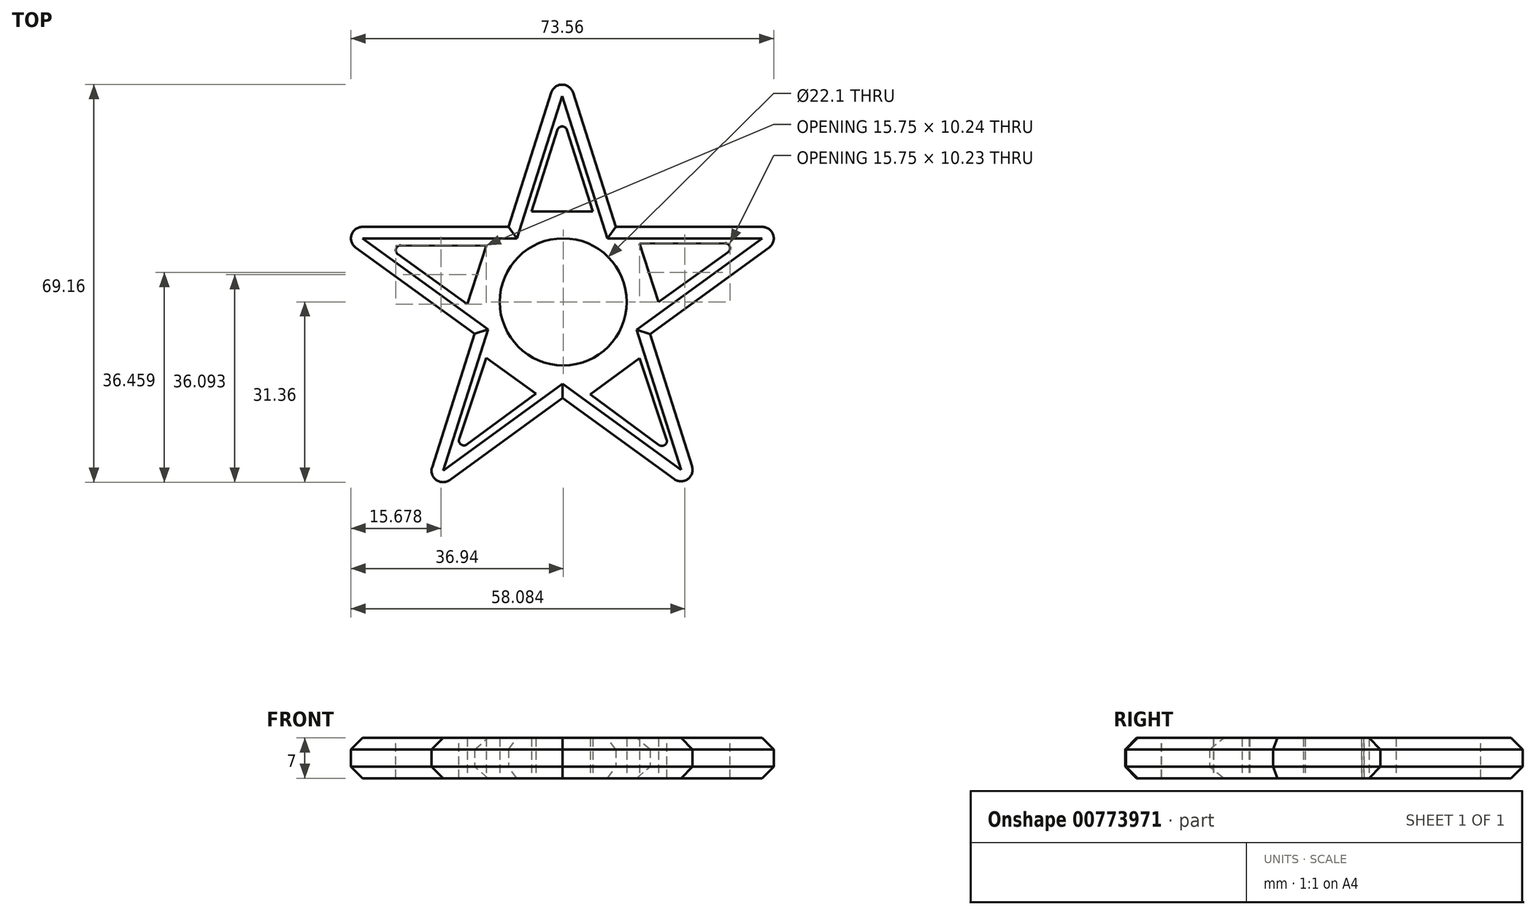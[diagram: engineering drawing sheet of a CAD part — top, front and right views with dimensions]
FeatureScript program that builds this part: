
annotation { "Feature Type Name" : "Feature", "Feature Type Description" : "" }
export const myFeature = defineFeature(function(context is Context, id is Id, definition is map)
    precondition{}
    {
        {
            var Q0;
            Q0=qCreatedBy(makeId("Top.planeOp"),FACE);
            var sketch = newSketch(context, id + "F0", { "sketchPlane" : qUnion([Q0])});
            skCircle(sketch, "E0", {"center": v(0, 0) * mm, "radius": 11.05 * mm});
            skLineSegment(sketch, "E1", {"start": v(-24.67, -34.57) * mm, "end": v(-0.2, 42.4) * mm});
            skLineSegment(sketch, "E2", {"start": v(-0.2, 42.4) * mm, "end": v(24.24, -34.41) * mm});
            skLineSegment(sketch, "E3", {"start": v(24.24, -34.41) * mm, "end": v(-41.1, 13.06) * mm});
            skLineSegment(sketch, "E4", {"start": v(-41.1, 13.06) * mm, "end": v(40.77, 13.06) * mm});
            skLineSegment(sketch, "E5", {"start": v(40.77, 13.06) * mm, "end": v(-24.67, -34.57) * mm});
            skLineSegment(sketch, "E6", {"start": v(-5.52, 15.75) * mm, "end": v(5.13, 15.75) * mm});
            skLineSegment(sketch, "E7", {"start": v(-0.2, 42.4) * mm, "end": v(-0.16, 11.05) * mm});
            skPoint(sketch, "E7.endSnap0", {"position": v(-0.16, 13.06) * mm});
            skLineSegment(sketch, "E8", {"start": v(-5.52, 15.75) * mm, "end": v(-0.19, 32.53) * mm});
            skLineSegment(sketch, "E9", {"start": v(-0.19, 32.53) * mm, "end": v(5.13, 15.75) * mm});
            skLineSegment(sketch, "E10.1.0", {"start": v(-31, 9.87) * mm, "end": v(-13.39, 9.75) * mm});
            skLineSegment(sketch, "E10.1.1", {"start": v(-16.68, -0.39) * mm, "end": v(-31, 9.87) * mm});
            skLineSegment(sketch, "E10.1.2", {"start": v(-16.68, -0.39) * mm, "end": v(-13.39, 9.75) * mm});
            skLineSegment(sketch, "E10.2.0", {"start": v(-18.97, -26.43) * mm, "end": v(-13.4, -9.72) * mm});
            skLineSegment(sketch, "E10.2.1", {"start": v(-4.79, -15.99) * mm, "end": v(-18.97, -26.43) * mm});
            skLineSegment(sketch, "E10.2.2", {"start": v(-4.79, -15.99) * mm, "end": v(-13.4, -9.72) * mm});
            skLineSegment(sketch, "E10.3.0", {"start": v(18.85, -26.52) * mm, "end": v(4.68, -16.07) * mm});
            skLineSegment(sketch, "E10.3.1", {"start": v(13.3, -9.8) * mm, "end": v(18.85, -26.52) * mm});
            skLineSegment(sketch, "E10.3.2", {"start": v(13.3, -9.8) * mm, "end": v(4.68, -16.07) * mm});
            skLineSegment(sketch, "E10.4.0", {"start": v(30.88, 10.23) * mm, "end": v(16.56, -0.02) * mm});
            skLineSegment(sketch, "E10.4.1", {"start": v(13.27, 10.12) * mm, "end": v(30.88, 10.23) * mm});
            skLineSegment(sketch, "E10.4.2", {"start": v(13.27, 10.12) * mm, "end": v(16.56, -0.02) * mm});
            skSolve(sketch);
        }
        {
            var Q0;
            Q0=qSketchRegion(id+"F0",true);
            extrude(context, id + "F1", {"entities" : qUnion([Q0]), "depth" : 7 * mm, "offsetDistance" : 25 * mm});
        }
        {
            var Q0;
            Q0=makeQuery(id+"F1.opExtrude","SWEPT_EDGE",EDGE,{"disambiguationData":[OSD([sQuery(id+"F0.wireOp",EDGE,"E1"),sQuery(id+"F0.wireOp",EDGE,"E2"),sQuery(id+"F0.wireOp",EDGE,"E7")])]});
            var Q1;
            Q1=makeQuery(id+"F1.opExtrude","SWEPT_EDGE",EDGE,{"disambiguationData":[OSD([sQuery(id+"F0.wireOp",EDGE,"E4"),sQuery(id+"F0.wireOp",EDGE,"E5")])]});
            var Q2;
            Q2=makeQuery(id+"F1.opExtrude","SWEPT_EDGE",EDGE,{"disambiguationData":[OSD([sQuery(id+"F0.wireOp",EDGE,"E2"),sQuery(id+"F0.wireOp",EDGE,"E3")])]});
            var Q3;
            Q3=makeQuery(id+"F1.opExtrude","SWEPT_EDGE",EDGE,{"disambiguationData":[OSD([sQuery(id+"F0.wireOp",EDGE,"E1"),sQuery(id+"F0.wireOp",EDGE,"E5")])]});
            var Q4;
            Q4=makeQuery(id+"F1.opExtrude","SWEPT_EDGE",EDGE,{"disambiguationData":[OSD([sQuery(id+"F0.wireOp",EDGE,"E3"),sQuery(id+"F0.wireOp",EDGE,"E4")])]});
            fillet(context, id + "F2", {"entities" : qUnion([Q0, Q1, Q2, Q3, Q4]), "radius" : 2 * mm, "tangentPropagation" : true, "allowEdgeOverflow" : false});
        }
        {
            var Q0;
            Q0=makeQuery(id+"F1.opExtrude","SWEPT_EDGE",EDGE,{"disambiguationData":[OSD([sQuery(id+"F0.wireOp",EDGE,"E10.2.0"),sQuery(id+"F0.wireOp",EDGE,"E10.2.1")])]});
            var Q1;
            Q1=makeQuery(id+"F1.opExtrude","SWEPT_EDGE",EDGE,{"disambiguationData":[OSD([sQuery(id+"F0.wireOp",EDGE,"E10.1.0"),sQuery(id+"F0.wireOp",EDGE,"E10.1.1")])]});
            var Q2;
            Q2=makeQuery(id+"F1.opExtrude","SWEPT_EDGE",EDGE,{"disambiguationData":[OSD([sQuery(id+"F0.wireOp",EDGE,"E10.3.0"),sQuery(id+"F0.wireOp",EDGE,"E10.3.1")])]});
            var Q3;
            Q3=makeQuery(id+"F1.opExtrude","SWEPT_EDGE",EDGE,{"disambiguationData":[OSD([sQuery(id+"F0.wireOp",EDGE,"E10.4.0"),sQuery(id+"F0.wireOp",EDGE,"E10.4.1")])]});
            var Q4;
            Q4=makeQuery(id+"F1.opExtrude","SWEPT_EDGE",EDGE,{"disambiguationData":[OSD([sQuery(id+"F0.wireOp",EDGE,"E7"),sQuery(id+"F0.wireOp",EDGE,"E8"),sQuery(id+"F0.wireOp",EDGE,"E9")])]});
            fillet(context, id + "F3", {"entities" : qUnion([Q0, Q1, Q2, Q3, Q4]), "radius" : 0.87 * mm, "tangentPropagation" : true, "allowEdgeOverflow" : false});
        }
        {
            var Q0;
            {var subQ0=sQuery(id+"F0.wireOp",EDGE,"E4");Q0=makeQuery(id+"F1.opExtrude","CAP_EDGE",EDGE,{"disambiguationData":[OSD([subQ0]),TDD([makeQuery(id+"F0.imprint","IMPRINT",EDGE,{"disambiguationData":[TD([[makeQuery(id+"F0.imprint","INTERSECT",VERTEX,{"derivedFrom":[sQuery(id+"F0.wireOp",EDGE,"E3"),subQ0]}),-1.0]])],"derivedFrom":subQ0})])],"isStart":false});}
            var Q1;
            {var subQ0=sQuery(id+"F0.wireOp",EDGE,"E1");Q1=makeQuery(id+"F1.opExtrude","CAP_EDGE",EDGE,{"disambiguationData":[OSD([subQ0]),TDD([makeQuery(id+"F0.imprint","IMPRINT",EDGE,{"disambiguationData":[TD([[makeQuery(id+"F0.imprint","INTERSECT",VERTEX,{"derivedFrom":[subQ0,sQuery(id+"F0.wireOp",EDGE,"E4")]}),-1.0]])],"derivedFrom":subQ0})])],"isStart":false});}
            var Q2;
            {var subQ0=sQuery(id+"F0.wireOp",EDGE,"E2");var subQ1=sQuery(id+"F0.wireOp",EDGE,"E1");Q2=makeQuery(id+"F2.opFillet","BLEND_EDGE",EDGE,{"blendedFrom":[makeQuery(id+"F1.opExtrude","SWEPT_EDGE",EDGE,{"disambiguationData":[OSD([subQ1,subQ0,sQuery(id+"F0.wireOp",EDGE,"E7")])]}),makeQuery(id+"F1.opExtrude","CAP_FACE",FACE,{"disambiguationData":[OSD([sQuery(id+"F0.wireOp",EDGE,"E0"),subQ1,subQ0,sQuery(id+"F0.wireOp",EDGE,"E3"),sQuery(id+"F0.wireOp",EDGE,"E4"),sQuery(id+"F0.wireOp",EDGE,"E5"),sQuery(id+"F0.wireOp",EDGE,"E6"),sQuery(id+"F0.wireOp",EDGE,"E8"),sQuery(id+"F0.wireOp",EDGE,"E9"),sQuery(id+"F0.wireOp",EDGE,"E10.1.0"),sQuery(id+"F0.wireOp",EDGE,"E10.1.1"),sQuery(id+"F0.wireOp",EDGE,"E10.1.2"),sQuery(id+"F0.wireOp",EDGE,"E10.2.0"),sQuery(id+"F0.wireOp",EDGE,"E10.2.1"),sQuery(id+"F0.wireOp",EDGE,"E10.2.2"),sQuery(id+"F0.wireOp",EDGE,"E10.3.0"),sQuery(id+"F0.wireOp",EDGE,"E10.3.1"),sQuery(id+"F0.wireOp",EDGE,"E10.3.2"),sQuery(id+"F0.wireOp",EDGE,"E10.4.0"),sQuery(id+"F0.wireOp",EDGE,"E10.4.1"),sQuery(id+"F0.wireOp",EDGE,"E10.4.2")])],"isStart":false})],"blendedInto":[makeQuery(id+"F1.opExtrude","CAP_FACE",FACE,{"disambiguationData":[OSD([sQuery(id+"F0.wireOp",EDGE,"E0"),subQ1,subQ0,sQuery(id+"F0.wireOp",EDGE,"E3"),sQuery(id+"F0.wireOp",EDGE,"E4"),sQuery(id+"F0.wireOp",EDGE,"E5"),sQuery(id+"F0.wireOp",EDGE,"E6"),sQuery(id+"F0.wireOp",EDGE,"E8"),sQuery(id+"F0.wireOp",EDGE,"E9"),sQuery(id+"F0.wireOp",EDGE,"E10.1.0"),sQuery(id+"F0.wireOp",EDGE,"E10.1.1"),sQuery(id+"F0.wireOp",EDGE,"E10.1.2"),sQuery(id+"F0.wireOp",EDGE,"E10.2.0"),sQuery(id+"F0.wireOp",EDGE,"E10.2.1"),sQuery(id+"F0.wireOp",EDGE,"E10.2.2"),sQuery(id+"F0.wireOp",EDGE,"E10.3.0"),sQuery(id+"F0.wireOp",EDGE,"E10.3.1"),sQuery(id+"F0.wireOp",EDGE,"E10.3.2"),sQuery(id+"F0.wireOp",EDGE,"E10.4.0"),sQuery(id+"F0.wireOp",EDGE,"E10.4.1"),sQuery(id+"F0.wireOp",EDGE,"E10.4.2")])],"isStart":false})]});}
            var Q3;
            {var subQ0=sQuery(id+"F0.wireOp",EDGE,"E2");Q3=makeQuery(id+"F1.opExtrude","CAP_EDGE",EDGE,{"disambiguationData":[OSD([subQ0]),TDD([makeQuery(id+"F0.imprint","IMPRINT",EDGE,{"disambiguationData":[TD([[makeQuery(id+"F0.imprint","INTERSECT",VERTEX,{"derivedFrom":[subQ0,sQuery(id+"F0.wireOp",EDGE,"E4")]}),1.0]])],"derivedFrom":subQ0})])],"isStart":false});}
            var Q4;
            {var subQ0=sQuery(id+"F0.wireOp",EDGE,"E4");Q4=makeQuery(id+"F1.opExtrude","CAP_EDGE",EDGE,{"disambiguationData":[OSD([subQ0]),TDD([makeQuery(id+"F0.imprint","IMPRINT",EDGE,{"disambiguationData":[TD([[makeQuery(id+"F0.imprint","INTERSECT",VERTEX,{"derivedFrom":[subQ0,sQuery(id+"F0.wireOp",EDGE,"E5")]}),1.0]])],"derivedFrom":subQ0})])],"isStart":false});}
            var Q5;
            {var subQ0=sQuery(id+"F0.wireOp",EDGE,"E5");var subQ1=sQuery(id+"F0.wireOp",EDGE,"E4");Q5=makeQuery(id+"F2.opFillet","BLEND_EDGE",EDGE,{"blendedFrom":[makeQuery(id+"F1.opExtrude","SWEPT_EDGE",EDGE,{"disambiguationData":[OSD([subQ1,subQ0])]}),makeQuery(id+"F1.opExtrude","CAP_FACE",FACE,{"disambiguationData":[OSD([sQuery(id+"F0.wireOp",EDGE,"E0"),sQuery(id+"F0.wireOp",EDGE,"E1"),sQuery(id+"F0.wireOp",EDGE,"E2"),sQuery(id+"F0.wireOp",EDGE,"E3"),subQ1,subQ0,sQuery(id+"F0.wireOp",EDGE,"E6"),sQuery(id+"F0.wireOp",EDGE,"E8"),sQuery(id+"F0.wireOp",EDGE,"E9"),sQuery(id+"F0.wireOp",EDGE,"E10.1.0"),sQuery(id+"F0.wireOp",EDGE,"E10.1.1"),sQuery(id+"F0.wireOp",EDGE,"E10.1.2"),sQuery(id+"F0.wireOp",EDGE,"E10.2.0"),sQuery(id+"F0.wireOp",EDGE,"E10.2.1"),sQuery(id+"F0.wireOp",EDGE,"E10.2.2"),sQuery(id+"F0.wireOp",EDGE,"E10.3.0"),sQuery(id+"F0.wireOp",EDGE,"E10.3.1"),sQuery(id+"F0.wireOp",EDGE,"E10.3.2"),sQuery(id+"F0.wireOp",EDGE,"E10.4.0"),sQuery(id+"F0.wireOp",EDGE,"E10.4.1"),sQuery(id+"F0.wireOp",EDGE,"E10.4.2")])],"isStart":false})],"blendedInto":[makeQuery(id+"F1.opExtrude","CAP_FACE",FACE,{"disambiguationData":[OSD([sQuery(id+"F0.wireOp",EDGE,"E0"),sQuery(id+"F0.wireOp",EDGE,"E1"),sQuery(id+"F0.wireOp",EDGE,"E2"),sQuery(id+"F0.wireOp",EDGE,"E3"),subQ1,subQ0,sQuery(id+"F0.wireOp",EDGE,"E6"),sQuery(id+"F0.wireOp",EDGE,"E8"),sQuery(id+"F0.wireOp",EDGE,"E9"),sQuery(id+"F0.wireOp",EDGE,"E10.1.0"),sQuery(id+"F0.wireOp",EDGE,"E10.1.1"),sQuery(id+"F0.wireOp",EDGE,"E10.1.2"),sQuery(id+"F0.wireOp",EDGE,"E10.2.0"),sQuery(id+"F0.wireOp",EDGE,"E10.2.1"),sQuery(id+"F0.wireOp",EDGE,"E10.2.2"),sQuery(id+"F0.wireOp",EDGE,"E10.3.0"),sQuery(id+"F0.wireOp",EDGE,"E10.3.1"),sQuery(id+"F0.wireOp",EDGE,"E10.3.2"),sQuery(id+"F0.wireOp",EDGE,"E10.4.0"),sQuery(id+"F0.wireOp",EDGE,"E10.4.1"),sQuery(id+"F0.wireOp",EDGE,"E10.4.2")])],"isStart":false})]});}
            var Q6;
            {var subQ0=sQuery(id+"F0.wireOp",EDGE,"E5");Q6=makeQuery(id+"F1.opExtrude","CAP_EDGE",EDGE,{"disambiguationData":[OSD([subQ0]),TDD([makeQuery(id+"F0.imprint","IMPRINT",EDGE,{"disambiguationData":[TD([[makeQuery(id+"F0.imprint","INTERSECT",VERTEX,{"derivedFrom":[sQuery(id+"F0.wireOp",EDGE,"E4"),subQ0]}),-1.0]])],"derivedFrom":subQ0})])],"isStart":false});}
            var Q7;
            {var subQ0=sQuery(id+"F0.wireOp",EDGE,"E2");Q7=makeQuery(id+"F1.opExtrude","CAP_EDGE",EDGE,{"disambiguationData":[OSD([subQ0]),TDD([makeQuery(id+"F0.imprint","IMPRINT",EDGE,{"disambiguationData":[TD([[makeQuery(id+"F0.imprint","INTERSECT",VERTEX,{"derivedFrom":[subQ0,sQuery(id+"F0.wireOp",EDGE,"E3")]}),1.0]])],"derivedFrom":subQ0})])],"isStart":false});}
            var Q8;
            {var subQ0=sQuery(id+"F0.wireOp",EDGE,"E3");var subQ1=sQuery(id+"F0.wireOp",EDGE,"E2");Q8=makeQuery(id+"F2.opFillet","BLEND_EDGE",EDGE,{"blendedFrom":[makeQuery(id+"F1.opExtrude","SWEPT_EDGE",EDGE,{"disambiguationData":[OSD([subQ1,subQ0])]}),makeQuery(id+"F1.opExtrude","CAP_FACE",FACE,{"disambiguationData":[OSD([sQuery(id+"F0.wireOp",EDGE,"E0"),sQuery(id+"F0.wireOp",EDGE,"E1"),subQ1,subQ0,sQuery(id+"F0.wireOp",EDGE,"E4"),sQuery(id+"F0.wireOp",EDGE,"E5"),sQuery(id+"F0.wireOp",EDGE,"E6"),sQuery(id+"F0.wireOp",EDGE,"E8"),sQuery(id+"F0.wireOp",EDGE,"E9"),sQuery(id+"F0.wireOp",EDGE,"E10.1.0"),sQuery(id+"F0.wireOp",EDGE,"E10.1.1"),sQuery(id+"F0.wireOp",EDGE,"E10.1.2"),sQuery(id+"F0.wireOp",EDGE,"E10.2.0"),sQuery(id+"F0.wireOp",EDGE,"E10.2.1"),sQuery(id+"F0.wireOp",EDGE,"E10.2.2"),sQuery(id+"F0.wireOp",EDGE,"E10.3.0"),sQuery(id+"F0.wireOp",EDGE,"E10.3.1"),sQuery(id+"F0.wireOp",EDGE,"E10.3.2"),sQuery(id+"F0.wireOp",EDGE,"E10.4.0"),sQuery(id+"F0.wireOp",EDGE,"E10.4.1"),sQuery(id+"F0.wireOp",EDGE,"E10.4.2")])],"isStart":false})],"blendedInto":[makeQuery(id+"F1.opExtrude","CAP_FACE",FACE,{"disambiguationData":[OSD([sQuery(id+"F0.wireOp",EDGE,"E0"),sQuery(id+"F0.wireOp",EDGE,"E1"),subQ1,subQ0,sQuery(id+"F0.wireOp",EDGE,"E4"),sQuery(id+"F0.wireOp",EDGE,"E5"),sQuery(id+"F0.wireOp",EDGE,"E6"),sQuery(id+"F0.wireOp",EDGE,"E8"),sQuery(id+"F0.wireOp",EDGE,"E9"),sQuery(id+"F0.wireOp",EDGE,"E10.1.0"),sQuery(id+"F0.wireOp",EDGE,"E10.1.1"),sQuery(id+"F0.wireOp",EDGE,"E10.1.2"),sQuery(id+"F0.wireOp",EDGE,"E10.2.0"),sQuery(id+"F0.wireOp",EDGE,"E10.2.1"),sQuery(id+"F0.wireOp",EDGE,"E10.2.2"),sQuery(id+"F0.wireOp",EDGE,"E10.3.0"),sQuery(id+"F0.wireOp",EDGE,"E10.3.1"),sQuery(id+"F0.wireOp",EDGE,"E10.3.2"),sQuery(id+"F0.wireOp",EDGE,"E10.4.0"),sQuery(id+"F0.wireOp",EDGE,"E10.4.1"),sQuery(id+"F0.wireOp",EDGE,"E10.4.2")])],"isStart":false})]});}
            var Q9;
            {var subQ0=sQuery(id+"F0.wireOp",EDGE,"E3");Q9=makeQuery(id+"F1.opExtrude","CAP_EDGE",EDGE,{"disambiguationData":[OSD([subQ0]),TDD([makeQuery(id+"F0.imprint","IMPRINT",EDGE,{"disambiguationData":[TD([[makeQuery(id+"F0.imprint","INTERSECT",VERTEX,{"derivedFrom":[sQuery(id+"F0.wireOp",EDGE,"E2"),subQ0]}),-1.0]])],"derivedFrom":subQ0})])],"isStart":false});}
            var Q10;
            {var subQ0=sQuery(id+"F0.wireOp",EDGE,"E5");Q10=makeQuery(id+"F1.opExtrude","CAP_EDGE",EDGE,{"disambiguationData":[OSD([subQ0]),TDD([makeQuery(id+"F0.imprint","IMPRINT",EDGE,{"disambiguationData":[TD([[makeQuery(id+"F0.imprint","INTERSECT",VERTEX,{"derivedFrom":[sQuery(id+"F0.wireOp",EDGE,"E1"),subQ0]}),1.0]])],"derivedFrom":subQ0})])],"isStart":false});}
            var Q11;
            {var subQ0=sQuery(id+"F0.wireOp",EDGE,"E1");Q11=makeQuery(id+"F1.opExtrude","CAP_EDGE",EDGE,{"disambiguationData":[OSD([subQ0]),TDD([makeQuery(id+"F0.imprint","IMPRINT",EDGE,{"disambiguationData":[TD([[makeQuery(id+"F0.imprint","INTERSECT",VERTEX,{"derivedFrom":[subQ0,sQuery(id+"F0.wireOp",EDGE,"E5")]}),-1.0]])],"derivedFrom":subQ0})])],"isStart":false});}
            var Q12;
            {var subQ0=sQuery(id+"F0.wireOp",EDGE,"E3");Q12=makeQuery(id+"F1.opExtrude","CAP_EDGE",EDGE,{"disambiguationData":[OSD([subQ0]),TDD([makeQuery(id+"F0.imprint","IMPRINT",EDGE,{"disambiguationData":[TD([[makeQuery(id+"F0.imprint","INTERSECT",VERTEX,{"derivedFrom":[subQ0,sQuery(id+"F0.wireOp",EDGE,"E4")]}),1.0]])],"derivedFrom":subQ0})])],"isStart":false});}
            var Q13;
            {var subQ0=sQuery(id+"F0.wireOp",EDGE,"E4");var subQ1=sQuery(id+"F0.wireOp",EDGE,"E3");Q13=makeQuery(id+"F2.opFillet","BLEND_EDGE",EDGE,{"blendedFrom":[makeQuery(id+"F1.opExtrude","SWEPT_EDGE",EDGE,{"disambiguationData":[OSD([subQ1,subQ0])]}),makeQuery(id+"F1.opExtrude","CAP_FACE",FACE,{"disambiguationData":[OSD([sQuery(id+"F0.wireOp",EDGE,"E0"),sQuery(id+"F0.wireOp",EDGE,"E1"),sQuery(id+"F0.wireOp",EDGE,"E2"),subQ1,subQ0,sQuery(id+"F0.wireOp",EDGE,"E5"),sQuery(id+"F0.wireOp",EDGE,"E6"),sQuery(id+"F0.wireOp",EDGE,"E8"),sQuery(id+"F0.wireOp",EDGE,"E9"),sQuery(id+"F0.wireOp",EDGE,"E10.1.0"),sQuery(id+"F0.wireOp",EDGE,"E10.1.1"),sQuery(id+"F0.wireOp",EDGE,"E10.1.2"),sQuery(id+"F0.wireOp",EDGE,"E10.2.0"),sQuery(id+"F0.wireOp",EDGE,"E10.2.1"),sQuery(id+"F0.wireOp",EDGE,"E10.2.2"),sQuery(id+"F0.wireOp",EDGE,"E10.3.0"),sQuery(id+"F0.wireOp",EDGE,"E10.3.1"),sQuery(id+"F0.wireOp",EDGE,"E10.3.2"),sQuery(id+"F0.wireOp",EDGE,"E10.4.0"),sQuery(id+"F0.wireOp",EDGE,"E10.4.1"),sQuery(id+"F0.wireOp",EDGE,"E10.4.2")])],"isStart":false})],"blendedInto":[makeQuery(id+"F1.opExtrude","CAP_FACE",FACE,{"disambiguationData":[OSD([sQuery(id+"F0.wireOp",EDGE,"E0"),sQuery(id+"F0.wireOp",EDGE,"E1"),sQuery(id+"F0.wireOp",EDGE,"E2"),subQ1,subQ0,sQuery(id+"F0.wireOp",EDGE,"E5"),sQuery(id+"F0.wireOp",EDGE,"E6"),sQuery(id+"F0.wireOp",EDGE,"E8"),sQuery(id+"F0.wireOp",EDGE,"E9"),sQuery(id+"F0.wireOp",EDGE,"E10.1.0"),sQuery(id+"F0.wireOp",EDGE,"E10.1.1"),sQuery(id+"F0.wireOp",EDGE,"E10.1.2"),sQuery(id+"F0.wireOp",EDGE,"E10.2.0"),sQuery(id+"F0.wireOp",EDGE,"E10.2.1"),sQuery(id+"F0.wireOp",EDGE,"E10.2.2"),sQuery(id+"F0.wireOp",EDGE,"E10.3.0"),sQuery(id+"F0.wireOp",EDGE,"E10.3.1"),sQuery(id+"F0.wireOp",EDGE,"E10.3.2"),sQuery(id+"F0.wireOp",EDGE,"E10.4.0"),sQuery(id+"F0.wireOp",EDGE,"E10.4.1"),sQuery(id+"F0.wireOp",EDGE,"E10.4.2")])],"isStart":false})]});}
            chamfer(context, id + "F4", {"entities" : qUnion([Q0, Q1, Q2, Q3, Q4, Q5, Q6, Q7, Q8, Q9, Q10, Q11, Q12, Q13]), "width" : 2 * mm, "tangentPropagation" : true});
        }
        {
            var Q0;
            {var subQ0=sQuery(id+"F0.wireOp",EDGE,"E4");Q0=makeQuery(id+"F1.opExtrude","CAP_EDGE",EDGE,{"disambiguationData":[OSD([subQ0]),TDD([makeQuery(id+"F0.imprint","IMPRINT",EDGE,{"disambiguationData":[TD([[makeQuery(id+"F0.imprint","INTERSECT",VERTEX,{"derivedFrom":[subQ0,sQuery(id+"F0.wireOp",EDGE,"E5")]}),1.0]])],"derivedFrom":subQ0})])],"isStart":true});}
            var Q1;
            {var subQ0=sQuery(id+"F0.wireOp",EDGE,"E2");Q1=makeQuery(id+"F1.opExtrude","CAP_EDGE",EDGE,{"disambiguationData":[OSD([subQ0]),TDD([makeQuery(id+"F0.imprint","IMPRINT",EDGE,{"disambiguationData":[TD([[makeQuery(id+"F0.imprint","INTERSECT",VERTEX,{"derivedFrom":[subQ0,sQuery(id+"F0.wireOp",EDGE,"E4")]}),1.0]])],"derivedFrom":subQ0})])],"isStart":true});}
            var Q2;
            {var subQ0=sQuery(id+"F0.wireOp",EDGE,"E1");Q2=makeQuery(id+"F1.opExtrude","CAP_EDGE",EDGE,{"disambiguationData":[OSD([subQ0]),TDD([makeQuery(id+"F0.imprint","IMPRINT",EDGE,{"disambiguationData":[TD([[makeQuery(id+"F0.imprint","INTERSECT",VERTEX,{"derivedFrom":[subQ0,sQuery(id+"F0.wireOp",EDGE,"E4")]}),-1.0]])],"derivedFrom":subQ0})])],"isStart":true});}
            var Q3;
            {var subQ0=sQuery(id+"F0.wireOp",EDGE,"E4");Q3=makeQuery(id+"F1.opExtrude","CAP_EDGE",EDGE,{"disambiguationData":[OSD([subQ0]),TDD([makeQuery(id+"F0.imprint","IMPRINT",EDGE,{"disambiguationData":[TD([[makeQuery(id+"F0.imprint","INTERSECT",VERTEX,{"derivedFrom":[sQuery(id+"F0.wireOp",EDGE,"E3"),subQ0]}),-1.0]])],"derivedFrom":subQ0})])],"isStart":true});}
            var Q4;
            {var subQ0=sQuery(id+"F0.wireOp",EDGE,"E3");Q4=makeQuery(id+"F1.opExtrude","CAP_EDGE",EDGE,{"disambiguationData":[OSD([subQ0]),TDD([makeQuery(id+"F0.imprint","IMPRINT",EDGE,{"disambiguationData":[TD([[makeQuery(id+"F0.imprint","INTERSECT",VERTEX,{"derivedFrom":[subQ0,sQuery(id+"F0.wireOp",EDGE,"E4")]}),1.0]])],"derivedFrom":subQ0})])],"isStart":true});}
            var Q5;
            {var subQ0=sQuery(id+"F0.wireOp",EDGE,"E1");Q5=makeQuery(id+"F1.opExtrude","CAP_EDGE",EDGE,{"disambiguationData":[OSD([subQ0]),TDD([makeQuery(id+"F0.imprint","IMPRINT",EDGE,{"disambiguationData":[TD([[makeQuery(id+"F0.imprint","INTERSECT",VERTEX,{"derivedFrom":[subQ0,sQuery(id+"F0.wireOp",EDGE,"E5")]}),-1.0]])],"derivedFrom":subQ0})])],"isStart":true});}
            var Q6;
            {var subQ0=sQuery(id+"F0.wireOp",EDGE,"E5");Q6=makeQuery(id+"F1.opExtrude","CAP_EDGE",EDGE,{"disambiguationData":[OSD([subQ0]),TDD([makeQuery(id+"F0.imprint","IMPRINT",EDGE,{"disambiguationData":[TD([[makeQuery(id+"F0.imprint","INTERSECT",VERTEX,{"derivedFrom":[sQuery(id+"F0.wireOp",EDGE,"E1"),subQ0]}),1.0]])],"derivedFrom":subQ0})])],"isStart":true});}
            var Q7;
            {var subQ0=sQuery(id+"F0.wireOp",EDGE,"E3");Q7=makeQuery(id+"F1.opExtrude","CAP_EDGE",EDGE,{"disambiguationData":[OSD([subQ0]),TDD([makeQuery(id+"F0.imprint","IMPRINT",EDGE,{"disambiguationData":[TD([[makeQuery(id+"F0.imprint","INTERSECT",VERTEX,{"derivedFrom":[sQuery(id+"F0.wireOp",EDGE,"E2"),subQ0]}),-1.0]])],"derivedFrom":subQ0})])],"isStart":true});}
            var Q8;
            {var subQ0=sQuery(id+"F0.wireOp",EDGE,"E5");Q8=makeQuery(id+"F1.opExtrude","CAP_EDGE",EDGE,{"disambiguationData":[OSD([subQ0]),TDD([makeQuery(id+"F0.imprint","IMPRINT",EDGE,{"disambiguationData":[TD([[makeQuery(id+"F0.imprint","INTERSECT",VERTEX,{"derivedFrom":[sQuery(id+"F0.wireOp",EDGE,"E4"),subQ0]}),-1.0]])],"derivedFrom":subQ0})])],"isStart":true});}
            var Q9;
            {var subQ0=sQuery(id+"F0.wireOp",EDGE,"E2");Q9=makeQuery(id+"F1.opExtrude","CAP_EDGE",EDGE,{"disambiguationData":[OSD([subQ0]),TDD([makeQuery(id+"F0.imprint","IMPRINT",EDGE,{"disambiguationData":[TD([[makeQuery(id+"F0.imprint","INTERSECT",VERTEX,{"derivedFrom":[subQ0,sQuery(id+"F0.wireOp",EDGE,"E3")]}),1.0]])],"derivedFrom":subQ0})])],"isStart":true});}
            var Q10;
            {var subQ0=sQuery(id+"F0.wireOp",EDGE,"E4");var subQ1=sQuery(id+"F0.wireOp",EDGE,"E3");Q10=makeQuery(id+"F2.opFillet","BLEND_EDGE",EDGE,{"blendedFrom":[makeQuery(id+"F1.opExtrude","SWEPT_EDGE",EDGE,{"disambiguationData":[OSD([subQ1,subQ0])]}),makeQuery(id+"F1.opExtrude","CAP_FACE",FACE,{"disambiguationData":[OSD([sQuery(id+"F0.wireOp",EDGE,"E0"),sQuery(id+"F0.wireOp",EDGE,"E1"),sQuery(id+"F0.wireOp",EDGE,"E2"),subQ1,subQ0,sQuery(id+"F0.wireOp",EDGE,"E5"),sQuery(id+"F0.wireOp",EDGE,"E6"),sQuery(id+"F0.wireOp",EDGE,"E8"),sQuery(id+"F0.wireOp",EDGE,"E9"),sQuery(id+"F0.wireOp",EDGE,"E10.1.0"),sQuery(id+"F0.wireOp",EDGE,"E10.1.1"),sQuery(id+"F0.wireOp",EDGE,"E10.1.2"),sQuery(id+"F0.wireOp",EDGE,"E10.2.0"),sQuery(id+"F0.wireOp",EDGE,"E10.2.1"),sQuery(id+"F0.wireOp",EDGE,"E10.2.2"),sQuery(id+"F0.wireOp",EDGE,"E10.3.0"),sQuery(id+"F0.wireOp",EDGE,"E10.3.1"),sQuery(id+"F0.wireOp",EDGE,"E10.3.2"),sQuery(id+"F0.wireOp",EDGE,"E10.4.0"),sQuery(id+"F0.wireOp",EDGE,"E10.4.1"),sQuery(id+"F0.wireOp",EDGE,"E10.4.2")])],"isStart":true})],"blendedInto":[makeQuery(id+"F1.opExtrude","CAP_FACE",FACE,{"disambiguationData":[OSD([sQuery(id+"F0.wireOp",EDGE,"E0"),sQuery(id+"F0.wireOp",EDGE,"E1"),sQuery(id+"F0.wireOp",EDGE,"E2"),subQ1,subQ0,sQuery(id+"F0.wireOp",EDGE,"E5"),sQuery(id+"F0.wireOp",EDGE,"E6"),sQuery(id+"F0.wireOp",EDGE,"E8"),sQuery(id+"F0.wireOp",EDGE,"E9"),sQuery(id+"F0.wireOp",EDGE,"E10.1.0"),sQuery(id+"F0.wireOp",EDGE,"E10.1.1"),sQuery(id+"F0.wireOp",EDGE,"E10.1.2"),sQuery(id+"F0.wireOp",EDGE,"E10.2.0"),sQuery(id+"F0.wireOp",EDGE,"E10.2.1"),sQuery(id+"F0.wireOp",EDGE,"E10.2.2"),sQuery(id+"F0.wireOp",EDGE,"E10.3.0"),sQuery(id+"F0.wireOp",EDGE,"E10.3.1"),sQuery(id+"F0.wireOp",EDGE,"E10.3.2"),sQuery(id+"F0.wireOp",EDGE,"E10.4.0"),sQuery(id+"F0.wireOp",EDGE,"E10.4.1"),sQuery(id+"F0.wireOp",EDGE,"E10.4.2")])],"isStart":true})]});}
            var Q11;
            {var subQ0=sQuery(id+"F0.wireOp",EDGE,"E2");var subQ1=sQuery(id+"F0.wireOp",EDGE,"E1");Q11=makeQuery(id+"F2.opFillet","BLEND_EDGE",EDGE,{"blendedFrom":[makeQuery(id+"F1.opExtrude","SWEPT_EDGE",EDGE,{"disambiguationData":[OSD([subQ1,subQ0,sQuery(id+"F0.wireOp",EDGE,"E7")])]}),makeQuery(id+"F1.opExtrude","CAP_FACE",FACE,{"disambiguationData":[OSD([sQuery(id+"F0.wireOp",EDGE,"E0"),subQ1,subQ0,sQuery(id+"F0.wireOp",EDGE,"E3"),sQuery(id+"F0.wireOp",EDGE,"E4"),sQuery(id+"F0.wireOp",EDGE,"E5"),sQuery(id+"F0.wireOp",EDGE,"E6"),sQuery(id+"F0.wireOp",EDGE,"E8"),sQuery(id+"F0.wireOp",EDGE,"E9"),sQuery(id+"F0.wireOp",EDGE,"E10.1.0"),sQuery(id+"F0.wireOp",EDGE,"E10.1.1"),sQuery(id+"F0.wireOp",EDGE,"E10.1.2"),sQuery(id+"F0.wireOp",EDGE,"E10.2.0"),sQuery(id+"F0.wireOp",EDGE,"E10.2.1"),sQuery(id+"F0.wireOp",EDGE,"E10.2.2"),sQuery(id+"F0.wireOp",EDGE,"E10.3.0"),sQuery(id+"F0.wireOp",EDGE,"E10.3.1"),sQuery(id+"F0.wireOp",EDGE,"E10.3.2"),sQuery(id+"F0.wireOp",EDGE,"E10.4.0"),sQuery(id+"F0.wireOp",EDGE,"E10.4.1"),sQuery(id+"F0.wireOp",EDGE,"E10.4.2")])],"isStart":true})],"blendedInto":[makeQuery(id+"F1.opExtrude","CAP_FACE",FACE,{"disambiguationData":[OSD([sQuery(id+"F0.wireOp",EDGE,"E0"),subQ1,subQ0,sQuery(id+"F0.wireOp",EDGE,"E3"),sQuery(id+"F0.wireOp",EDGE,"E4"),sQuery(id+"F0.wireOp",EDGE,"E5"),sQuery(id+"F0.wireOp",EDGE,"E6"),sQuery(id+"F0.wireOp",EDGE,"E8"),sQuery(id+"F0.wireOp",EDGE,"E9"),sQuery(id+"F0.wireOp",EDGE,"E10.1.0"),sQuery(id+"F0.wireOp",EDGE,"E10.1.1"),sQuery(id+"F0.wireOp",EDGE,"E10.1.2"),sQuery(id+"F0.wireOp",EDGE,"E10.2.0"),sQuery(id+"F0.wireOp",EDGE,"E10.2.1"),sQuery(id+"F0.wireOp",EDGE,"E10.2.2"),sQuery(id+"F0.wireOp",EDGE,"E10.3.0"),sQuery(id+"F0.wireOp",EDGE,"E10.3.1"),sQuery(id+"F0.wireOp",EDGE,"E10.3.2"),sQuery(id+"F0.wireOp",EDGE,"E10.4.0"),sQuery(id+"F0.wireOp",EDGE,"E10.4.1"),sQuery(id+"F0.wireOp",EDGE,"E10.4.2")])],"isStart":true})]});}
            var Q12;
            {var subQ0=sQuery(id+"F0.wireOp",EDGE,"E5");var subQ1=sQuery(id+"F0.wireOp",EDGE,"E4");Q12=makeQuery(id+"F2.opFillet","BLEND_EDGE",EDGE,{"blendedFrom":[makeQuery(id+"F1.opExtrude","SWEPT_EDGE",EDGE,{"disambiguationData":[OSD([subQ1,subQ0])]}),makeQuery(id+"F1.opExtrude","CAP_FACE",FACE,{"disambiguationData":[OSD([sQuery(id+"F0.wireOp",EDGE,"E0"),sQuery(id+"F0.wireOp",EDGE,"E1"),sQuery(id+"F0.wireOp",EDGE,"E2"),sQuery(id+"F0.wireOp",EDGE,"E3"),subQ1,subQ0,sQuery(id+"F0.wireOp",EDGE,"E6"),sQuery(id+"F0.wireOp",EDGE,"E8"),sQuery(id+"F0.wireOp",EDGE,"E9"),sQuery(id+"F0.wireOp",EDGE,"E10.1.0"),sQuery(id+"F0.wireOp",EDGE,"E10.1.1"),sQuery(id+"F0.wireOp",EDGE,"E10.1.2"),sQuery(id+"F0.wireOp",EDGE,"E10.2.0"),sQuery(id+"F0.wireOp",EDGE,"E10.2.1"),sQuery(id+"F0.wireOp",EDGE,"E10.2.2"),sQuery(id+"F0.wireOp",EDGE,"E10.3.0"),sQuery(id+"F0.wireOp",EDGE,"E10.3.1"),sQuery(id+"F0.wireOp",EDGE,"E10.3.2"),sQuery(id+"F0.wireOp",EDGE,"E10.4.0"),sQuery(id+"F0.wireOp",EDGE,"E10.4.1"),sQuery(id+"F0.wireOp",EDGE,"E10.4.2")])],"isStart":true})],"blendedInto":[makeQuery(id+"F1.opExtrude","CAP_FACE",FACE,{"disambiguationData":[OSD([sQuery(id+"F0.wireOp",EDGE,"E0"),sQuery(id+"F0.wireOp",EDGE,"E1"),sQuery(id+"F0.wireOp",EDGE,"E2"),sQuery(id+"F0.wireOp",EDGE,"E3"),subQ1,subQ0,sQuery(id+"F0.wireOp",EDGE,"E6"),sQuery(id+"F0.wireOp",EDGE,"E8"),sQuery(id+"F0.wireOp",EDGE,"E9"),sQuery(id+"F0.wireOp",EDGE,"E10.1.0"),sQuery(id+"F0.wireOp",EDGE,"E10.1.1"),sQuery(id+"F0.wireOp",EDGE,"E10.1.2"),sQuery(id+"F0.wireOp",EDGE,"E10.2.0"),sQuery(id+"F0.wireOp",EDGE,"E10.2.1"),sQuery(id+"F0.wireOp",EDGE,"E10.2.2"),sQuery(id+"F0.wireOp",EDGE,"E10.3.0"),sQuery(id+"F0.wireOp",EDGE,"E10.3.1"),sQuery(id+"F0.wireOp",EDGE,"E10.3.2"),sQuery(id+"F0.wireOp",EDGE,"E10.4.0"),sQuery(id+"F0.wireOp",EDGE,"E10.4.1"),sQuery(id+"F0.wireOp",EDGE,"E10.4.2")])],"isStart":true})]});}
            var Q13;
            {var subQ0=sQuery(id+"F0.wireOp",EDGE,"E3");var subQ1=sQuery(id+"F0.wireOp",EDGE,"E2");Q13=makeQuery(id+"F2.opFillet","BLEND_EDGE",EDGE,{"blendedFrom":[makeQuery(id+"F1.opExtrude","SWEPT_EDGE",EDGE,{"disambiguationData":[OSD([subQ1,subQ0])]}),makeQuery(id+"F1.opExtrude","CAP_FACE",FACE,{"disambiguationData":[OSD([sQuery(id+"F0.wireOp",EDGE,"E0"),sQuery(id+"F0.wireOp",EDGE,"E1"),subQ1,subQ0,sQuery(id+"F0.wireOp",EDGE,"E4"),sQuery(id+"F0.wireOp",EDGE,"E5"),sQuery(id+"F0.wireOp",EDGE,"E6"),sQuery(id+"F0.wireOp",EDGE,"E8"),sQuery(id+"F0.wireOp",EDGE,"E9"),sQuery(id+"F0.wireOp",EDGE,"E10.1.0"),sQuery(id+"F0.wireOp",EDGE,"E10.1.1"),sQuery(id+"F0.wireOp",EDGE,"E10.1.2"),sQuery(id+"F0.wireOp",EDGE,"E10.2.0"),sQuery(id+"F0.wireOp",EDGE,"E10.2.1"),sQuery(id+"F0.wireOp",EDGE,"E10.2.2"),sQuery(id+"F0.wireOp",EDGE,"E10.3.0"),sQuery(id+"F0.wireOp",EDGE,"E10.3.1"),sQuery(id+"F0.wireOp",EDGE,"E10.3.2"),sQuery(id+"F0.wireOp",EDGE,"E10.4.0"),sQuery(id+"F0.wireOp",EDGE,"E10.4.1"),sQuery(id+"F0.wireOp",EDGE,"E10.4.2")])],"isStart":true})],"blendedInto":[makeQuery(id+"F1.opExtrude","CAP_FACE",FACE,{"disambiguationData":[OSD([sQuery(id+"F0.wireOp",EDGE,"E0"),sQuery(id+"F0.wireOp",EDGE,"E1"),subQ1,subQ0,sQuery(id+"F0.wireOp",EDGE,"E4"),sQuery(id+"F0.wireOp",EDGE,"E5"),sQuery(id+"F0.wireOp",EDGE,"E6"),sQuery(id+"F0.wireOp",EDGE,"E8"),sQuery(id+"F0.wireOp",EDGE,"E9"),sQuery(id+"F0.wireOp",EDGE,"E10.1.0"),sQuery(id+"F0.wireOp",EDGE,"E10.1.1"),sQuery(id+"F0.wireOp",EDGE,"E10.1.2"),sQuery(id+"F0.wireOp",EDGE,"E10.2.0"),sQuery(id+"F0.wireOp",EDGE,"E10.2.1"),sQuery(id+"F0.wireOp",EDGE,"E10.2.2"),sQuery(id+"F0.wireOp",EDGE,"E10.3.0"),sQuery(id+"F0.wireOp",EDGE,"E10.3.1"),sQuery(id+"F0.wireOp",EDGE,"E10.3.2"),sQuery(id+"F0.wireOp",EDGE,"E10.4.0"),sQuery(id+"F0.wireOp",EDGE,"E10.4.1"),sQuery(id+"F0.wireOp",EDGE,"E10.4.2")])],"isStart":true})]});}
            var Q14;
            {var subQ0=sQuery(id+"F0.wireOp",EDGE,"E5");var subQ1=sQuery(id+"F0.wireOp",EDGE,"E1");Q14=makeQuery(id+"F2.opFillet","BLEND_EDGE",EDGE,{"blendedFrom":[makeQuery(id+"F1.opExtrude","SWEPT_EDGE",EDGE,{"disambiguationData":[OSD([subQ1,subQ0])]}),makeQuery(id+"F1.opExtrude","CAP_FACE",FACE,{"disambiguationData":[OSD([sQuery(id+"F0.wireOp",EDGE,"E0"),subQ1,sQuery(id+"F0.wireOp",EDGE,"E2"),sQuery(id+"F0.wireOp",EDGE,"E3"),sQuery(id+"F0.wireOp",EDGE,"E4"),subQ0,sQuery(id+"F0.wireOp",EDGE,"E6"),sQuery(id+"F0.wireOp",EDGE,"E8"),sQuery(id+"F0.wireOp",EDGE,"E9"),sQuery(id+"F0.wireOp",EDGE,"E10.1.0"),sQuery(id+"F0.wireOp",EDGE,"E10.1.1"),sQuery(id+"F0.wireOp",EDGE,"E10.1.2"),sQuery(id+"F0.wireOp",EDGE,"E10.2.0"),sQuery(id+"F0.wireOp",EDGE,"E10.2.1"),sQuery(id+"F0.wireOp",EDGE,"E10.2.2"),sQuery(id+"F0.wireOp",EDGE,"E10.3.0"),sQuery(id+"F0.wireOp",EDGE,"E10.3.1"),sQuery(id+"F0.wireOp",EDGE,"E10.3.2"),sQuery(id+"F0.wireOp",EDGE,"E10.4.0"),sQuery(id+"F0.wireOp",EDGE,"E10.4.1"),sQuery(id+"F0.wireOp",EDGE,"E10.4.2")])],"isStart":true})],"blendedInto":[makeQuery(id+"F1.opExtrude","CAP_FACE",FACE,{"disambiguationData":[OSD([sQuery(id+"F0.wireOp",EDGE,"E0"),subQ1,sQuery(id+"F0.wireOp",EDGE,"E2"),sQuery(id+"F0.wireOp",EDGE,"E3"),sQuery(id+"F0.wireOp",EDGE,"E4"),subQ0,sQuery(id+"F0.wireOp",EDGE,"E6"),sQuery(id+"F0.wireOp",EDGE,"E8"),sQuery(id+"F0.wireOp",EDGE,"E9"),sQuery(id+"F0.wireOp",EDGE,"E10.1.0"),sQuery(id+"F0.wireOp",EDGE,"E10.1.1"),sQuery(id+"F0.wireOp",EDGE,"E10.1.2"),sQuery(id+"F0.wireOp",EDGE,"E10.2.0"),sQuery(id+"F0.wireOp",EDGE,"E10.2.1"),sQuery(id+"F0.wireOp",EDGE,"E10.2.2"),sQuery(id+"F0.wireOp",EDGE,"E10.3.0"),sQuery(id+"F0.wireOp",EDGE,"E10.3.1"),sQuery(id+"F0.wireOp",EDGE,"E10.3.2"),sQuery(id+"F0.wireOp",EDGE,"E10.4.0"),sQuery(id+"F0.wireOp",EDGE,"E10.4.1"),sQuery(id+"F0.wireOp",EDGE,"E10.4.2")])],"isStart":true})]});}
            chamfer(context, id + "F5", {"entities" : qUnion([Q0, Q1, Q2, Q3, Q4, Q5, Q6, Q7, Q8, Q9, Q10, Q11, Q12, Q13, Q14]), "width" : 2 * mm, "tangentPropagation" : true});
        }
    });
